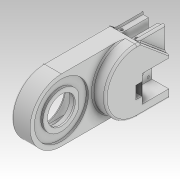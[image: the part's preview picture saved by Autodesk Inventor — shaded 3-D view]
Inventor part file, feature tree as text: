
AUTODESK INVENTOR PART (.ipt)
format: ipt  version: 2020 (Build 240168000, 168)  size: 801,280 bytes
history: native  units: mm
features: sketch x32, extrude x30, chamfer x4, fillet x3, plane x2, revolve x2, projected_geometry x1
ambient origin geometry x8: Origin, YZ Plane, XZ Plane, XY Plane, X Axis, Y Axis, Z Axis, Center Point
bodies: Solid1 (feature_tree)
feature tree (74):
  extrude  "Extrusion1"  Depth=250.0mm
  extrude  "Extrusion3"  Depth=50.0mm TaperAngle=0.0deg
  extrude  "Extrusion6"  TaperAngle=0.0deg  [1 undecoded]
  extrude  "Extrusion7"  Depth=8.726646mm
  extrude  "Extrusion8"  Depth=10.0mm TaperAngle=0.0deg
  extrude  "Extrusion9"  TaperAngle=0.0deg  [1 undecoded]
  extrude  "Extrusion10"  TaperAngle=30.0deg  [1 undecoded]
  extrude  "Extrusion11"  Depth=16.15mm
  extrude  "Extrusion12"  Depth=60.0mm
  plane  "Work Plane1"
  extrude  "Extrusion13"  Depth=10.0mm TaperAngle=0.0deg
  revolve  "Revolution1"  [1 undecoded]
  extrude  "Extrusion14"  Depth=86.0mm
  extrude  "Extrusion15"  Depth=3.5mm TaperAngle=0.0deg
  extrude  "Extrusion16"  Depth=75.0mm
  revolve  "Revolution2"  [1 undecoded]
  extrude  "Extrusion17"  Depth=7.3mm
  fillet  "Fillet1"  [1 undecoded]
  plane  "Work Plane2"
  extrude  "Extrusion18"  Depth=31.0mm
  extrude  "Extrusion19"  Depth=3.0mm TaperAngle=0.0deg
  extrude  "Extrusion20"  Depth=15.0mm TaperAngle=0.0deg
  extrude  "Extrusion21"  Depth=15.0mm
  extrude  "Extrusion25"  Depth=6.0mm TaperAngle=360.0deg
  extrude  "Extrusion22"  Depth=15.0mm
  fillet  "Fillet2"  Radius=5.2mm
  fillet  "Fillet3"  Radius=1.0mm
  extrude  "Extrusion23"  TaperAngle=90.0deg  [1 undecoded]
  extrude  "Extrusion24"  Depth=20.0mm
  extrude  "Extrusion26"  Depth=19.198622mm
  extrude  "Extrusion27"  Depth=15.0mm
  extrude  "Extrusion28"  TaperAngle=0.0deg  [1 undecoded]
  extrude  "CHOP"  Depth=8.0mm
  extrude  "Extrusion30"  Depth=12.5mm
  extrude  "Extrusion31"  Depth=2.45mm
  extrude  "Extrusion32"  Depth=10.0mm
  chamfer  "Chamfer1"  Distance=110.0mm
  chamfer  "Chamfer2"  Distance=3.0mm
  chamfer  "Chamfer3"  Distance=3.0mm
  chamfer  "Chamfer4"  Distance=5.0mm
  extrude  "Extrusion33"  Depth=0.2mm
  sketch  "Sketch1"  dims[d0=50.0mm d1=250.0mm]
  sketch  "Sketch3"  dims[d2=47.2mm d3=50.0mm d4=0.0mm]
  sketch  "Sketch6"  dims[d10=5.0mm d11=0.0mm d12=0.0mm]
  sketch  "Sketch7"  dims[d19=50.0mm d20=0.0mm d21=8.726646mm]
  projected_geometry  "Projected Loop1"
  sketch  "Sketch8"  dims[d22=75.0mm d25=10.0mm d26=0.0mm]
  sketch  "Sketch9"  dims[d27=50.0mm d30=0.0mm d31=0.0mm]
  sketch  "Sketch10"  dims[d33=30.0deg d34=30.0deg]
  sketch  "Sketch11"  dims[d35=0.0mm d36=0.0mm d37=16.15mm]
  sketch  "Sketch12"  dims[d38=3.3mm d39=60.0mm]
  sketch  "Sketch13"  dims[d40=80.0mm d42=360.0deg d44=10.0mm d45=0.0mm]
  sketch  "Sketch14"  dims[d50=42.5mm d51=42.5mm d52=0.0mm d53=0.0mm]
  sketch  "Sketch15"  dims[d54=38.0mm d55=86.0mm]
  sketch  "Sketch16"  dims[d56=59.0mm d57=3.5mm d58=0.0mm]
  sketch  "Sketch17"  dims[d59=-2.0mm d60=75.0mm]
  sketch  "Sketch18"  dims[d61=40.0mm d62=18.0mm d63=0.0mm]
  sketch  "Sketch19"  dims[d64=1.5mm d65=7.3mm d66=90.0deg]
  sketch  "Sketch20"  dims[d67=22.0mm d68=31.0mm]
  sketch  "Sketch21"  dims[d69=3.5mm d70=3.0mm d71=0.0mm]
  sketch  "Sketch22"  dims[d72=0.0mm d73=15.0mm d74=0.0mm]
  sketch  "Sketch23"  dims[d75=15.0mm d76=130.0mm]
  sketch  "Sketch24"  dims[d77=6.0mm d78=80.0mm d80=360.0deg]
  sketch  "Sketch25"  dims[d82=15.0mm d83=0.0mm d84=5.2mm d85=5.2mm d86=1.0mm]
  sketch  "Sketch26"  dims[d87=1.5mm d88=90.0deg]
  sketch  "Sketch27"  dims[d89=5.5mm d90=20.0mm]
  sketch  "Sketch28"  dims[d91=30.0deg d92=19.198622mm]
  sketch  "Sketch29"  dims[d93=15.0mm d94=0.0mm d95=50.0mm]
  sketch  "Sketch30"  dims[d96=30.0mm d97=0.0mm]
  sketch  "Sketch31"  dims[d98=8.0mm d99=14.0mm]
  sketch  "Sketch32"  dims[d100=6.4mm d101=12.5mm]
  sketch  "Sketch33"  dims[d102=130.0mm d103=80.0mm d104=0.0mm d105=0.0mm d106=2.45mm]
  sketch  "Sketch34"  dims[d107=10.0mm d108=10.0mm]
  sketch  "Sketch35"  dims[d109=32.0mm d110=110.0mm d111=0.0mm d112=3.0mm d113=3.0mm d114=5.0mm d115=1.0mm d116=4.0mm d117=0.0mm d118=4.0mm d119=4.0mm d120=32.25mm d121=0.0mm d122=3.0mm d124=0.5mm d125=0.0mm d126=3.0mm d127=2.0mm d128=8.0mm d129=8.0mm d130=4.0mm d131=4.0mm d132=4.3mm d133=6.0mm d134=0.0mm d135=4.0mm d136=0.0mm d137=70.0mm d138=0.5mm d139=0.0mm d140=2.5mm d141=10.0mm d142=20.0mm d143=15.0mm d144=0.0mm d145=8.0mm d146=23.75mm d147=0.0mm d148=15.0mm d149=23.75mm d150=0.0mm d151=200.998mm d152=0.0mm d153=0.0mm d154=0.0mm d155=5.0mm d156=2.0mm d157=45.0deg d158=10.0mm d159=3.5mm d160=0.0mm d161=0.8mm d162=2.0mm d163=45.0deg d164=6.108652mm d165=37.0mm d166=0.0mm d167=0.5mm d168=2.0mm d169=45.0deg d170=10.0mm d171=2.0mm d172=45.0deg d173=0.2mm d174=0.0mm d123=0.872665mm]
note: 8 required parameter values undecoded (feature->parameter linkage not recoverable at this tier; creation-order binding heuristic only, values carry confidence <= 0.55)